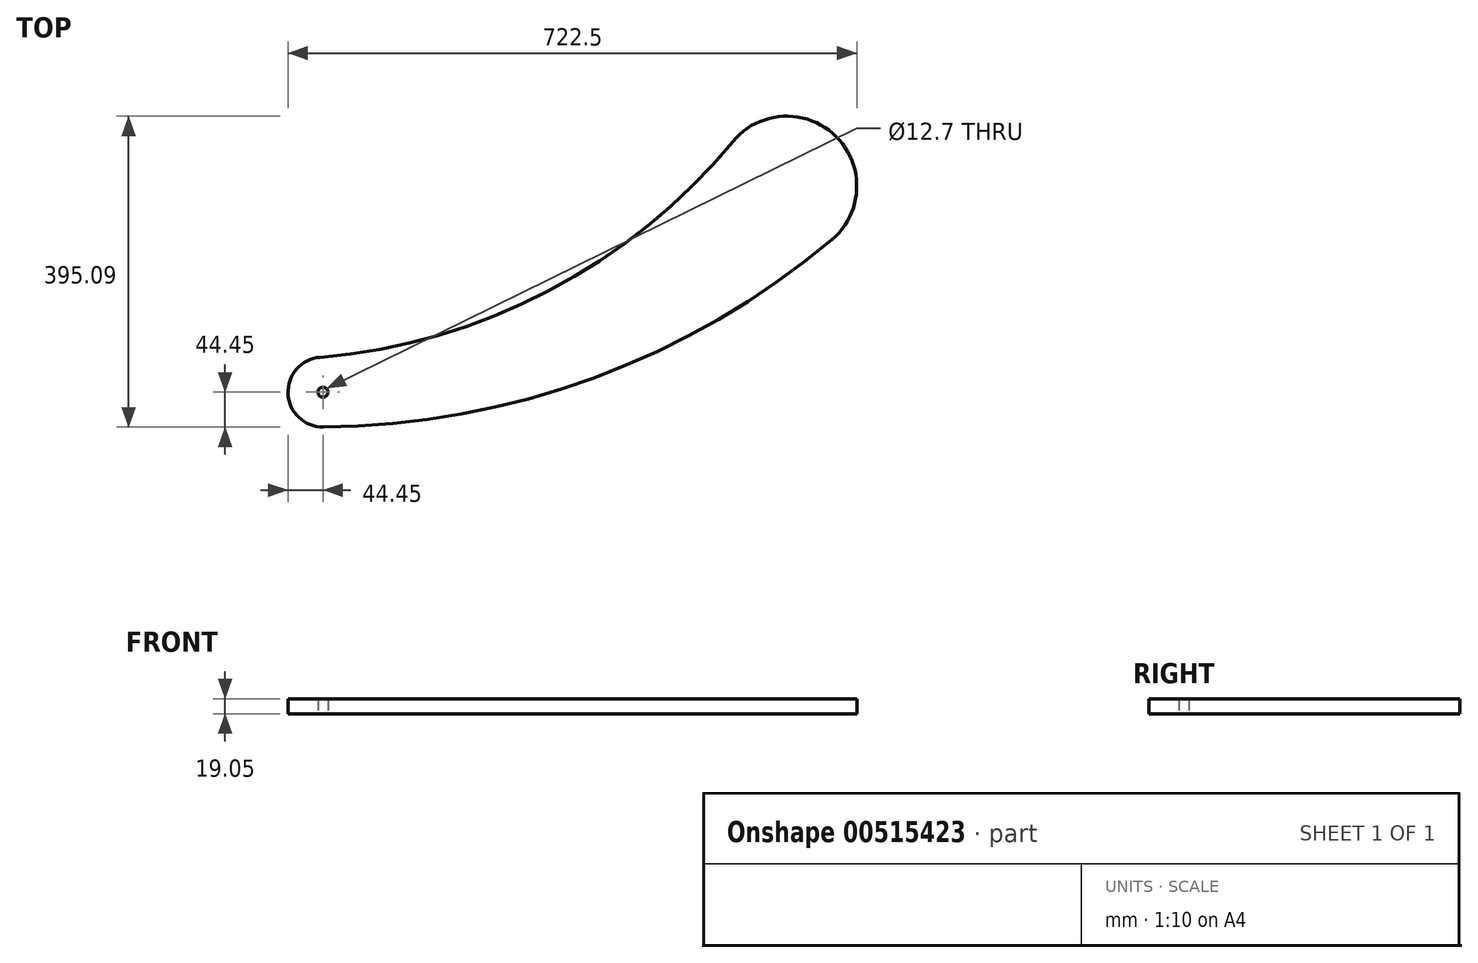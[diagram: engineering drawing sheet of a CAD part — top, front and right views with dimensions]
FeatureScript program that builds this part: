
annotation { "Feature Type Name" : "Feature", "Feature Type Description" : "" }
export const myFeature = defineFeature(function(context is Context, id is Id, definition is map)
    precondition{}
    {
        {
            var Q0;
            Q0=qCreatedBy(makeId("Top.planeOp"),FACE);
            var sketch = newSketch(context, id + "F0", { "sketchPlane" : qUnion([Q0])});
            skCircle(sketch, "E0", {"center": v(0, 0) * mm, "radius": 44.45 * mm});
            skCircle(sketch, "E1", {"center": v(589.15, 261.74) * mm, "radius": 88.9 * mm});
            skArc(sketch, "E2", {"start": v(0.33, -44.45) * mm, "mid": v(344.12, 18.22) * mm, "end": v(646.34, 193.68) * mm});
            skArc(sketch, "E3", {"start": v(-3.68, 44.3) * mm, "mid": v(286.15, 128.37) * mm, "end": v(520.61, 318.36) * mm});
            skCircle(sketch, "E4", {"center": v(0, 0) * mm, "radius": 127 * mm, "construction": true});
            skCircle(sketch, "E5", {"center": v(711.2, 0) * mm, "radius": 127 * mm, "construction": true});
            skLineSegment(sketch, "E6", {"start": v(0, 0) * mm, "end": v(711.2, 0) * mm, "construction": true});
            skLineSegment(sketch, "E7", {"start": v(711.2, 0) * mm, "end": v(711.2, 127) * mm, "construction": true});
            skLineSegment(sketch, "E8", {"start": v(711.2, 0) * mm, "end": v(589.15, 261.74) * mm, "construction": true});
            skLineSegment(sketch, "E9", {"start": v(0, -127) * mm, "end": v(711.2, -127) * mm, "construction": true});
            skLineSegment(sketch, "E10", {"start": v(150.22, 203.2) * mm, "end": v(402.27, 203.2) * mm, "construction": true});
            skCircle(sketch, "E11", {"center": v(0, 0) * mm, "radius": 6.35 * mm});
            skSolve(sketch);
        }
        {
            var Q0;
            Q0=makeQuery(id+"F0.imprint","IMPRINT",FACE,{"disambiguationData":[TD([[makeQuery(id+"F0.imprint","IMPRINT",EDGE,{"derivedFrom":sQuery(id+"F0.wireOp",EDGE,"E11")}),-1.0]])]});
            var Q1;
            {var subQ0=sQuery(id+"F0.wireOp",EDGE,"E1");var subQ1=makeQuery(id+"F0.imprint","INTERSECT",VERTEX,{"derivedFrom":[subQ0,sQuery(id+"F0.wireOp",EDGE,"E2")]});Q1=makeQuery(id+"F0.imprint","IMPRINT",FACE,{"disambiguationData":[TD([[makeQuery(id+"F0.imprint","IMPRINT",EDGE,{"disambiguationData":[TD([[subQ1,1.0]])],"derivedFrom":subQ0}),1.0]])]});}
            var Q2;
            {var subQ0=sQuery(id+"F0.wireOp",EDGE,"E2");Q2=makeQuery(id+"F0.imprint","IMPRINT",FACE,{"disambiguationData":[TD([[makeQuery(id+"F0.imprint","IMPRINT",EDGE,{"derivedFrom":subQ0}),1.0]])]});}
            extrude(context, id + "F1", {"entities" : qUnion([Q0, Q1, Q2]), "depth" : 19.05 * mm, "offsetDistance" : 25.4 * mm});
        }
    });
